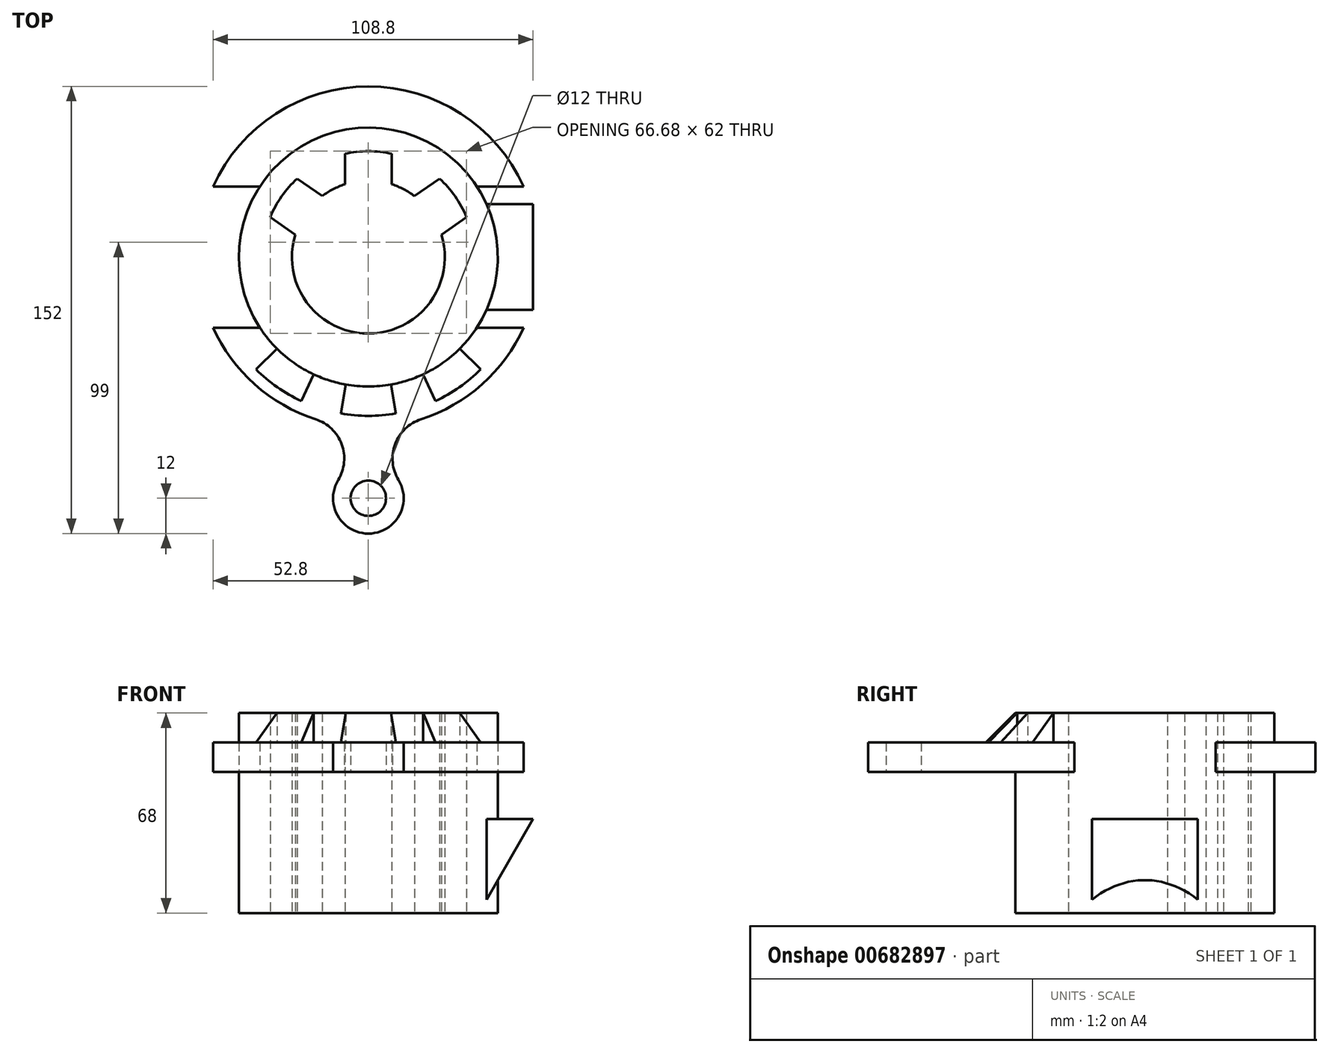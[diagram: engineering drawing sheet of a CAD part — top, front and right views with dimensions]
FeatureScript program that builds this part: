
annotation { "Feature Type Name" : "Feature", "Feature Type Description" : "" }
export const myFeature = defineFeature(function(context is Context, id is Id, definition is map)
    precondition{}
    {
        {
            var Q0;
            Q0=qCreatedBy(makeId("Top.planeOp"),FACE);
            var sketch = newSketch(context, id + "F0", { "sketchPlane" : qUnion([Q0])});
            skCircle(sketch, "E0", {"center": v(0, 0) * mm, "radius": 44 * mm});
            skCircle(sketch, "E1", {"center": v(0, 0) * mm, "radius": 36 * mm});
            skArc(sketch, "E2", {"start": v(-24.85, 7.64) * mm, "mid": v(0, -26) * mm, "end": v(24.85, 7.64) * mm});
            skLineSegment(sketch, "E3.left", {"start": v(8, 35.1) * mm, "end": v(8, 24.74) * mm});
            skLineSegment(sketch, "E3.right", {"start": v(-8, 35.1) * mm, "end": v(-8, 24.74) * mm});
            skPoint(sketch, "E3.middle", {"position": v(0, 26) * mm});
            skLineSegment(sketch, "E4", {"start": v(0, 0) * mm, "end": v(0, 56.03) * mm});
            skLineSegment(sketch, "E5.MirrorCS", {"start": v(24.16, 26.69) * mm, "end": v(15.68, 20.74) * mm});
            skLineSegment(sketch, "E6.MirrorCS", {"start": v(33.34, 13.58) * mm, "end": v(24.85, 7.64) * mm});
            skLineSegment(sketch, "E7.MirrorCS", {"start": v(-24.16, 26.69) * mm, "end": v(-15.68, 20.74) * mm});
            skLineSegment(sketch, "E8.MirrorCS", {"start": v(-33.34, 13.58) * mm, "end": v(-24.85, 7.64) * mm});
            skArc(sketch, "E9.trimOffspring", {"start": v(-8, 24.74) * mm, "mid": v(-12, 23.06) * mm, "end": v(-15.68, 20.74) * mm});
            skArc(sketch, "E10.trimOffspring", {"start": v(15.68, 20.74) * mm, "mid": v(12, 23.06) * mm, "end": v(8, 24.74) * mm});
            skSolve(sketch);
        }
        {
            var Q0;
            Q0 = qSketchRegion(id + "F0", true);
            var Q1;
            Q1=makeQuery(id+"F0.imprint","IMPRINT",FACE,{"disambiguationData":[TD([[makeQuery(id+"F0.imprint","IMPRINT",EDGE,{"derivedFrom":sQuery(id+"F0.wireOp",EDGE,"E2")}),-1.0]])]});
            var Q2;
            {var subQ0=sQuery(id+"F0.wireOp",EDGE,"E3.right");Q2=makeQuery(id+"F0.imprint","IMPRINT",FACE,{"disambiguationData":[TD([[makeQuery(id+"F0.imprint","IMPRINT",EDGE,{"derivedFrom":subQ0}),-1.0]])]});}
            var Q3;
            {var subQ0=sQuery(id+"F0.wireOp",EDGE,"E3.left");Q3=makeQuery(id+"F0.imprint","IMPRINT",FACE,{"disambiguationData":[TD([[makeQuery(id+"F0.imprint","IMPRINT",EDGE,{"derivedFrom":subQ0}),1.0]])]});}
            extrude(context, id + "F1", {"entities" : qUnion([Q0, Q1, Q2, Q3]), "depth" : 68 * mm, "offsetDistance" : 25 * mm});
        }
        {
            var Q0;
            Q0=qCreatedBy(makeId("Top.planeOp"),FACE);
            cPlane(context, id + "F2", {"entities" : qUnion([Q0]), "cplaneType" : CPlaneType.OFFSET, "offset" : 48 * mm, "width" : 150 * mm, "height" : 150 * mm});
        }
        {
            var Q0;
            Q0=qCreatedBy(id+"F2.planeOp",FACE);
            var sketch = newSketch(context, id + "F3", { "sketchPlane" : qUnion([Q0])});
            skArc(sketch, "E11", {"start": v(52.8, 24) * mm, "mid": v(0, 58) * mm, "end": v(-52.8, 24) * mm});
            skLineSegment(sketch, "E12", {"start": v(0, 0) * mm, "end": v(0, 24) * mm});
            skLineSegment(sketch, "E13", {"start": v(0, 24) * mm, "end": v(52.8, 24) * mm});
            skLineSegment(sketch, "E14", {"start": v(0, 0) * mm, "end": v(0, -24) * mm});
            skLineSegment(sketch, "E15", {"start": v(0, -24) * mm, "end": v(52.8, -24) * mm});
            skLineSegment(sketch, "E16", {"start": v(0, -24) * mm, "end": v(-52.8, -24) * mm});
            skLineSegment(sketch, "E17", {"start": v(0, 24) * mm, "end": v(-52.8, 24) * mm});
            skArc(sketch, "E18.trimOffspring", {"start": v(-52.8, -24) * mm, "mid": v(0, -58) * mm, "end": v(52.8, -24) * mm});
            skLineSegment(sketch, "E19", {"start": v(0, 0) * mm, "end": v(0, -82) * mm});
            skCircle(sketch, "E20", {"center": v(0, -82) * mm, "radius": 6 * mm});
            skCircle(sketch, "E21", {"center": v(0, -82) * mm, "radius": 12 * mm});
            skArc(sketch, "E22", {"start": v(17.9, -55.17) * mm, "mid": v(9.09, -63.62) * mm, "end": v(10.25, -75.76) * mm});
            skArc(sketch, "E23", {"start": v(-10.25, -75.76) * mm, "mid": v(-9.09, -63.62) * mm, "end": v(-17.9, -55.17) * mm});
            skCircle(sketch, "E24", {"center": v(0, 0) * mm, "radius": 44 * mm});
            skSolve(sketch);
        }
        {
            var Q0;
            {var subQ0=sQuery(id+"F3.wireOp",EDGE,"E22");Q0=makeQuery(id+"F3.imprint","IMPRINT",FACE,{"disambiguationData":[TD([[makeQuery(id+"F3.imprint","IMPRINT",EDGE,{"derivedFrom":subQ0}),-1.0]])]});}
            var Q1;
            {var subQ0=sQuery(id+"F3.wireOp",EDGE,"E23");Q1=makeQuery(id+"F3.imprint","IMPRINT",FACE,{"disambiguationData":[TD([[makeQuery(id+"F3.imprint","IMPRINT",EDGE,{"derivedFrom":subQ0}),-1.0]])]});}
            var Q2;
            Q2=makeQuery(id+"F3.imprint","IMPRINT",FACE,{"disambiguationData":[TD([[makeQuery(id+"F3.imprint","IMPRINT",EDGE,{"derivedFrom":sQuery(id+"F3.wireOp",EDGE,"E20")}),-1.0]])]});
            var Q3;
            Q3=makeQuery(id+"F3.imprint","IMPRINT",FACE,{"disambiguationData":[TD([[makeQuery(id+"F3.imprint","IMPRINT",EDGE,{"derivedFrom":sQuery(id+"F3.wireOp",EDGE,"E11")}),1.0]])]});
            var Q4;
            {var subQ1=sQuery(id+"F3.wireOp",EDGE,"E18.trimOffspring");var subQ6=sQuery(id+"F3.wireOp",EDGE,"E16");var subQ7=makeQuery(id+"F3.imprint","INTERSECT",VERTEX,{"derivedFrom":[subQ6,subQ1]});Q4=makeQuery(id+"F3.imprint","IMPRINT",FACE,{"disambiguationData":[TD([[makeQuery(id+"F3.imprint","IMPRINT",EDGE,{"disambiguationData":[TD([[subQ7,1.0]])],"derivedFrom":subQ6}),1.0]])]});}
            var Q5;
            {var subQ1=sQuery(id+"F3.wireOp",EDGE,"E18.trimOffspring");var subQ5=sQuery(id+"F3.wireOp",EDGE,"E15");var subQ6=makeQuery(id+"F3.imprint","INTERSECT",VERTEX,{"derivedFrom":[subQ5,subQ1]});Q5=makeQuery(id+"F3.imprint","IMPRINT",FACE,{"disambiguationData":[TD([[makeQuery(id+"F3.imprint","IMPRINT",EDGE,{"disambiguationData":[TD([[subQ6,1.0]])],"derivedFrom":subQ5}),-1.0]])]});}
            extrude(context, id + "F4", {"entities" : qUnion([Q0, Q1, Q2, Q3, Q4, Q5]), "operationType" : NewBodyOperationType.ADD, "depth" : 10 * mm, "offsetDistance" : 25 * mm});
        }
        {
            var Q0;
            Q0=qCreatedBy(makeId("Top.planeOp"),FACE);
            cPlane(context, id + "F5", {"entities" : qUnion([Q0]), "cplaneType" : CPlaneType.OFFSET, "offset" : 32 * mm, "width" : 150 * mm, "height" : 150 * mm});
        }
        {
            var Q0;
            Q0=qCreatedBy(id+"F5.planeOp",FACE);
            var sketch = newSketch(context, id + "F6", { "sketchPlane" : qUnion([Q0])});
            skArc(sketch, "E25", {"start": v(40.15, -18) * mm, "mid": v(44, 0) * mm, "end": v(40.15, 18) * mm});
            skLineSegment(sketch, "E26", {"start": v(40.15, -18) * mm, "end": v(56, -18) * mm});
            skLineSegment(sketch, "E27", {"start": v(44, 0) * mm, "end": v(56, 0) * mm});
            skLineSegment(sketch, "E28", {"start": v(56, 0) * mm, "end": v(56, -18) * mm});
            skLineSegment(sketch, "E29", {"start": v(56, -18) * mm, "end": v(56, 18) * mm});
            skLineSegment(sketch, "E30", {"start": v(56, 18) * mm, "end": v(40.15, 18) * mm});
            skPoint(sketch, "E31.orphan", {"position": v(6, -18) * mm});
            skPoint(sketch, "E32.right.end.orphan", {"position": v(-6, -18) * mm});
            skPoint(sketch, "E32.bottom.end.orphan", {"position": v(-6, 18) * mm});
            skPoint(sketch, "E33.orphan", {"position": v(6, 18) * mm});
            skSolve(sketch);
        }
        {
            var Q0;
            Q0=sQuery(id+"F6.wireOp",EDGE,"E26");
            cPlane(context, id + "F7", {"entities" : qUnion([Q0]), "cplaneType" : CPlaneType.LINE_ANGLE, "offset" : 25 * mm, "angle" : 0 * degree, "width" : 150 * mm, "height" : 150 * mm});
        }
        {
            var Q0;
            Q0=qCreatedBy(id+"F7.planeOp",FACE);
            var sketch = newSketch(context, id + "F8", { "sketchPlane" : qUnion([Q0])});
            skLineSegment(sketch, "E34", {"start": v(-56, 32) * mm, "end": v(-62.16, 32) * mm});
            skLineSegment(sketch, "E35", {"start": v(-56, 32) * mm, "end": v(-39.47, 3.37) * mm});
            skLineSegment(sketch, "E36", {"start": v(-39.47, 3.37) * mm, "end": v(-39.47, 32) * mm});
            skLineSegment(sketch, "E37", {"start": v(-39.47, 32) * mm, "end": v(-56, 32) * mm});
            skSolve(sketch);
        }
        {
            var Q0;
            Q0=makeQuery(id+"F8.imprint","IMPRINT",FACE,{"disambiguationData":[TD([[makeQuery(id+"F8.imprint","IMPRINT",EDGE,{"derivedFrom":sQuery(id+"F8.wireOp",EDGE,"p1Br3cpP-qGL9-1H0n-rLs3-fDpTSQRY340k")}),-1.0]])]});
            var Q1;
            Q1=makeQuery(id+"F8.imprint","IMPRINT",FACE,{"disambiguationData":[TD([[makeQuery(id+"F8.imprint","IMPRINT",EDGE,{"derivedFrom":sQuery(id+"F8.wireOp",EDGE,"E35")}),1.0]])]});
            extrude(context, id + "F9", {"entities" : qUnion([Q0, Q1]), "operationType" : NewBodyOperationType.ADD, "depth" : 36 * mm, "offsetDistance" : 25 * mm});
        }
        {
            var Q0;
            Q0=makeQuery(id+"F4.opExtrude","CAP_FACE",FACE,{"disambiguationData":[OSD([sQuery(id+"F3.wireOp",EDGE,"E15"),sQuery(id+"F3.wireOp",EDGE,"E16"),sQuery(id+"F3.wireOp",EDGE,"E18.trimOffspring"),sQuery(id+"F3.wireOp",EDGE,"E20"),sQuery(id+"F3.wireOp",EDGE,"E21"),sQuery(id+"F3.wireOp",EDGE,"E22"),sQuery(id+"F3.wireOp",EDGE,"E23"),sQuery(id+"F3.wireOp",EDGE,"E24")])],"isStart":false});
            var sketch = newSketch(context, id + "F10", { "sketchPlane" : qUnion([Q0])});
            skLineSegment(sketch, "E38", {"start": v(0, 0) * mm, "end": v(0, -54) * mm});
            skLineSegment(sketch, "E39", {"start": v(0, 0) * mm, "end": v(-9.38, -53.18) * mm});
            skLineSegment(sketch, "E40.MirrorCS", {"start": v(0, 0) * mm, "end": v(9.38, -53.18) * mm});
            skLineSegment(sketch, "E41", {"start": v(0, 0) * mm, "end": v(-22.82, -48.94) * mm});
            skLineSegment(sketch, "E42", {"start": v(0, 0) * mm, "end": v(-38.18, -38.18) * mm});
            skLineSegment(sketch, "E43", {"start": v(0, 0) * mm, "end": v(22.82, -48.94) * mm});
            skLineSegment(sketch, "E44", {"start": v(0, 0) * mm, "end": v(38.18, -38.18) * mm});
            skArc(sketch, "E45", {"start": v(-38.18, -38.18) * mm, "mid": v(-30.97, -44.23) * mm, "end": v(-22.82, -48.94) * mm});
            skPoint(sketch, "E46.orphan", {"position": v(-16.16, -91.67) * mm});
            skPoint(sketch, "E47.orphan", {"position": v(16.16, -91.67) * mm});
            skArc(sketch, "E48.trimOffspring", {"start": v(-9.38, -53.18) * mm, "mid": v(0, -54) * mm, "end": v(9.38, -53.18) * mm});
            skArc(sketch, "E49.trimOffspring", {"start": v(22.82, -48.94) * mm, "mid": v(30.97, -44.23) * mm, "end": v(38.18, -38.18) * mm});
            skSolve(sketch);
        }
        {
            var Q0;
            {var subQ0=sQuery(id+"F10.wireOp",EDGE,"E45");Q0=makeQuery(id+"F10.imprint","IMPRINT",FACE,{"disambiguationData":[TD([[makeQuery(id+"F10.imprint","IMPRINT",EDGE,{"derivedFrom":subQ0}),1.0]])]});}
            var Q1;
            {var subQ0=sQuery(id+"F10.wireOp",EDGE,"E48.trimOffspring");var subQ1=sQuery(id+"F10.wireOp",EDGE,"E38");var subQ2=makeQuery(id+"F10.imprint","INTERSECT",VERTEX,{"derivedFrom":[subQ1,subQ0]});Q1=makeQuery(id+"F10.imprint","IMPRINT",FACE,{"disambiguationData":[TD([[makeQuery(id+"F10.imprint","IMPRINT",EDGE,{"disambiguationData":[TD([[subQ2,1.0]])],"derivedFrom":subQ0}),1.0]])]});}
            var Q2;
            {var subQ0=sQuery(id+"F10.wireOp",EDGE,"E48.trimOffspring");var subQ1=sQuery(id+"F10.wireOp",EDGE,"E38");var subQ2=makeQuery(id+"F10.imprint","INTERSECT",VERTEX,{"derivedFrom":[subQ1,subQ0]});Q2=makeQuery(id+"F10.imprint","IMPRINT",FACE,{"disambiguationData":[TD([[makeQuery(id+"F10.imprint","IMPRINT",EDGE,{"disambiguationData":[TD([[subQ2,-1.0]])],"derivedFrom":subQ0}),1.0]])]});}
            var Q3;
            {var subQ0=sQuery(id+"F10.wireOp",EDGE,"E49.trimOffspring");Q3=makeQuery(id+"F10.imprint","IMPRINT",FACE,{"disambiguationData":[TD([[makeQuery(id+"F10.imprint","IMPRINT",EDGE,{"derivedFrom":subQ0}),1.0]])]});}
            extrude(context, id + "F11", {"entities" : qUnion([Q0, Q1, Q2, Q3]), "operationType" : NewBodyOperationType.ADD, "depth" : 10 * mm, "offsetDistance" : 25 * mm});
        }
        {
            var Q0;
            Q0=makeQuery(id+"F11.opExtrude","CAP_EDGE",EDGE,{"disambiguationData":[OSD([sQuery(id+"F10.wireOp",EDGE,"E45")])],"isStart":false});
            var Q1;
            Q1=makeQuery(id+"F11.opExtrude","CAP_EDGE",EDGE,{"disambiguationData":[OSD([sQuery(id+"F10.wireOp",EDGE,"E48.trimOffspring")])],"isStart":false});
            var Q2;
            Q2=makeQuery(id+"F11.opExtrude","CAP_EDGE",EDGE,{"disambiguationData":[OSD([sQuery(id+"F10.wireOp",EDGE,"E49.trimOffspring")])],"isStart":false});
            chamfer(context, id + "F12", {"entities" : qUnion([Q0, Q1, Q2]), "width" : 10 * mm, "tangentPropagation" : true});
        }
    });
